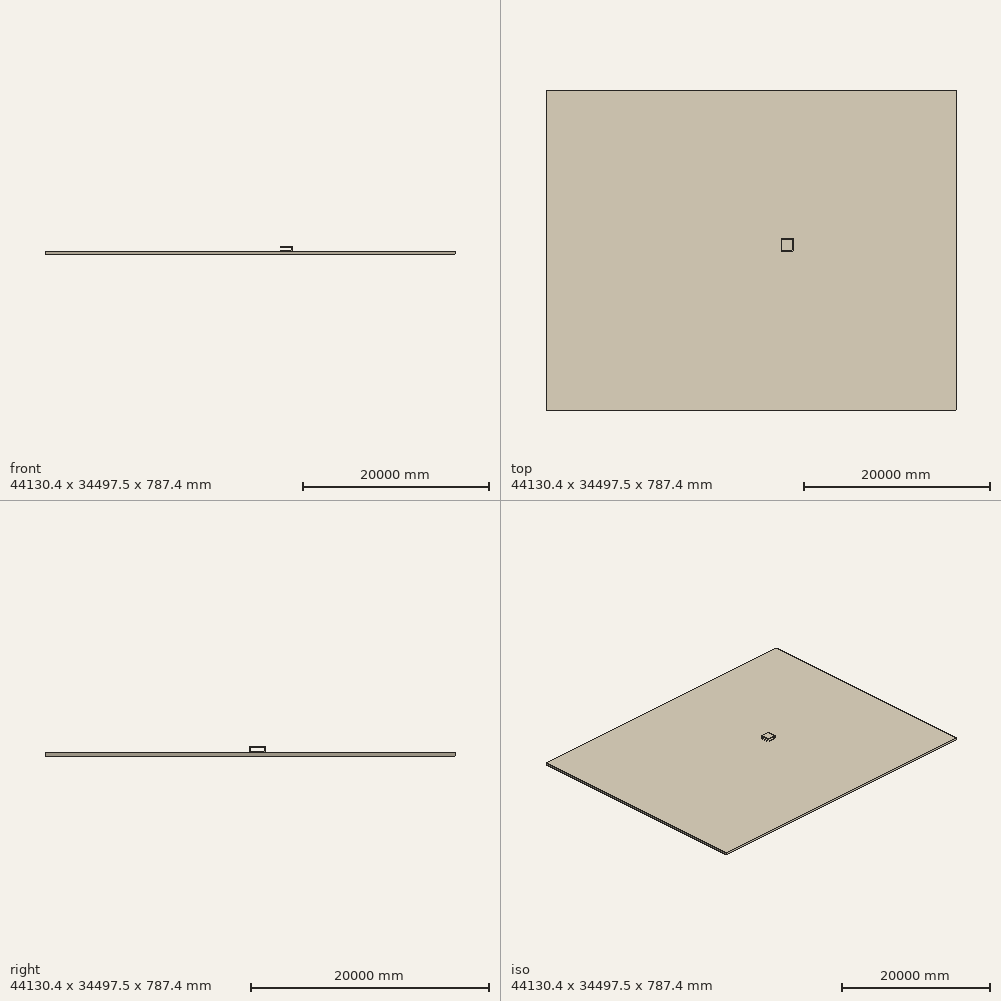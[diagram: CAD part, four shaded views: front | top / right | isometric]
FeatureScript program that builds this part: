
annotation { "Feature Type Name" : "Feature", "Feature Type Description" : "" }
export const myFeature = defineFeature(function(context is Context, id is Id, definition is map)
    precondition{}
    {
        {
            var Q0;
            Q0=qCreatedBy(makeId("Top.planeOp"),FACE);
            var sketch = newSketch(context, id + "F0", { "sketchPlane" : qUnion([Q0])});
            skLineSegment(sketch, "E0", {"start": v(0, 0) * mm, "end": v(0, 1320.8) * mm});
            skLineSegment(sketch, "E1", {"start": v(0, 0) * mm, "end": v(1301.47, 0) * mm});
            skLineSegment(sketch, "E2", {"start": v(0, 1320.8) * mm, "end": v(1301.47, 1320.8) * mm});
            skLineSegment(sketch, "E3", {"start": v(1301.47, 1320.8) * mm, "end": v(1301.47, 0) * mm});
            skLineSegment(sketch, "E4", {"start": v(50.8, 50.8) * mm, "end": v(1250.67, 50.8) * mm});
            skLineSegment(sketch, "E5", {"start": v(1250.67, 50.8) * mm, "end": v(1250.67, 1270) * mm});
            skLineSegment(sketch, "E6", {"start": v(1250.67, 1270) * mm, "end": v(50.8, 1270) * mm});
            skLineSegment(sketch, "E7", {"start": v(50.8, 1270) * mm, "end": v(50.8, 50.8) * mm});
            skLineSegment(sketch, "E8", {"start": v(387.94, 1270) * mm, "end": v(387.94, 1320.8) * mm, "construction": true});
            skLineSegment(sketch, "E9", {"start": v(1250.67, 761.64) * mm, "end": v(1301.47, 761.64) * mm, "construction": true});
            skLineSegment(sketch, "E10", {"start": v(50.8, 721.4) * mm, "end": v(0, 721.4) * mm, "construction": true});
            skLineSegment(sketch, "E11", {"start": v(704.11, 50.8) * mm, "end": v(704.11, 0) * mm, "construction": true});
            skSolve(sketch);
        }
        {
            var Q0;
            Q0=makeQuery(id+"F0.imprint","IMPRINT",FACE,{"disambiguationData":[TD([[makeQuery(id+"F0.imprint","IMPRINT",EDGE,{"derivedFrom":sQuery(id+"F0.wireOp",EDGE,"E0")}),-1.0]])]});
            extrude(context, id + "F1", {"entities" : qUnion([Q0]), "depth" : 50.8 * mm});
        }
        {
            var Q0;
            Q0=makeQuery(id+"F1.opExtrude","CAP_FACE",FACE,{"disambiguationData":[OSD([sQuery(id+"F0.wireOp",EDGE,"E0"),sQuery(id+"F0.wireOp",EDGE,"E1"),sQuery(id+"F0.wireOp",EDGE,"E2"),sQuery(id+"F0.wireOp",EDGE,"E3"),sQuery(id+"F0.wireOp",EDGE,"E4"),sQuery(id+"F0.wireOp",EDGE,"E5"),sQuery(id+"F0.wireOp",EDGE,"E6"),sQuery(id+"F0.wireOp",EDGE,"E7")])],"isStart":false});
            var sketch = newSketch(context, id + "F2", { "sketchPlane" : qUnion([Q0])});
            skLineSegment(sketch, "E12", {"start": v(1250.67, 50.8) * mm, "end": v(1250.67, 0) * mm});
            skLineSegment(sketch, "E13", {"start": v(1301.47, 0) * mm, "end": v(1250.67, 0) * mm});
            skLineSegment(sketch, "E14", {"start": v(1250.67, 50.8) * mm, "end": v(1301.47, 50.8) * mm});
            skLineSegment(sketch, "E15", {"start": v(1301.47, 0) * mm, "end": v(1301.47, 50.8) * mm});
            skLineSegment(sketch, "E16", {"start": v(1250.67, 1270) * mm, "end": v(1301.47, 1270) * mm});
            skLineSegment(sketch, "E17", {"start": v(1301.47, 1320.8) * mm, "end": v(1301.47, 1270) * mm});
            skLineSegment(sketch, "E18", {"start": v(1301.47, 1320.8) * mm, "end": v(1250.67, 1320.8) * mm});
            skLineSegment(sketch, "E19", {"start": v(1250.67, 1270) * mm, "end": v(1250.67, 1320.8) * mm});
            skLineSegment(sketch, "E20", {"start": v(0, 1320.8) * mm, "end": v(50.8, 1320.8) * mm});
            skLineSegment(sketch, "E21", {"start": v(50.8, 1270) * mm, "end": v(50.8, 1320.8) * mm});
            skLineSegment(sketch, "E22", {"start": v(50.8, 1270) * mm, "end": v(0, 1270) * mm});
            skLineSegment(sketch, "E23", {"start": v(0, 1320.8) * mm, "end": v(0, 1270) * mm});
            skLineSegment(sketch, "E24", {"start": v(50.8, 50.8) * mm, "end": v(0, 50.8) * mm});
            skLineSegment(sketch, "E25", {"start": v(0, 50.8) * mm, "end": v(0, 0) * mm});
            skLineSegment(sketch, "E26", {"start": v(0, 0) * mm, "end": v(50.8, 0) * mm});
            skLineSegment(sketch, "E27", {"start": v(50.8, 0) * mm, "end": v(50.8, 50.8) * mm});
            skSolve(sketch);
        }
        {
            var Q0;
            Q0=makeQuery(id+"F2.imprint","IMPRINT",FACE,{"disambiguationData":[TD([[makeQuery(id+"F2.imprint","IMPRINT",EDGE,{"derivedFrom":sQuery(id+"F2.wireOp",EDGE,"E24")}),1.0]])]});
            var Q1;
            Q1=makeQuery(id+"F2.imprint","IMPRINT",FACE,{"disambiguationData":[TD([[makeQuery(id+"F2.imprint","IMPRINT",EDGE,{"derivedFrom":sQuery(id+"F2.wireOp",EDGE,"E20")}),-1.0]])]});
            var Q2;
            Q2=makeQuery(id+"F2.imprint","IMPRINT",FACE,{"disambiguationData":[TD([[makeQuery(id+"F2.imprint","IMPRINT",EDGE,{"derivedFrom":sQuery(id+"F2.wireOp",EDGE,"E16")}),1.0]])]});
            var Q3;
            Q3=makeQuery(id+"F2.imprint","IMPRINT",FACE,{"disambiguationData":[TD([[makeQuery(id+"F2.imprint","IMPRINT",EDGE,{"derivedFrom":sQuery(id+"F2.wireOp",EDGE,"E12")}),1.0]])]});
            extrude(context, id + "F3", {"entities" : qUnion([Q0, Q1, Q2, Q3]), "operationType" : NewBodyOperationType.ADD, "depth" : 355.6 * mm});
        }
        {
            var Q0;
            Q0=makeQuery(id+"F3.opExtrude","CAP_FACE",FACE,{"disambiguationData":[OSD([sQuery(id+"F2.wireOp",EDGE,"E24"),sQuery(id+"F2.wireOp",EDGE,"E25"),sQuery(id+"F2.wireOp",EDGE,"E26"),sQuery(id+"F2.wireOp",EDGE,"E27")])],"isStart":false});
            var sketch = newSketch(context, id + "F4", { "sketchPlane" : qUnion([Q0])});
            skSolve(sketch);
        }
        {
            var Q0;
            Q0=makeQuery(id+"F4.imprint","IMPRINT",FACE,{"disambiguationData":[TD([[makeQuery(id+"F4.imprint","IMPRINT",EDGE,{"derivedFrom":makeQuery(id+"F3.opExtrude","CAP_EDGE",EDGE,{"disambiguationData":[OSD([sQuery(id+"F2.wireOp",EDGE,"E24")])],"isStart":false})}),1.0]])]});
            var sketch = newSketch(context, id + "F5", { "sketchPlane" : qUnion([Q0])});
            skLineSegment(sketch, "E28.bottom", {"start": v(0, 0) * mm, "end": v(1301.47, 0) * mm});
            skLineSegment(sketch, "E28.top", {"start": v(0, 1320.8) * mm, "end": v(1301.47, 1320.8) * mm});
            skLineSegment(sketch, "E28.left", {"start": v(0, 0) * mm, "end": v(0, 1320.8) * mm});
            skLineSegment(sketch, "E28.right", {"start": v(1301.47, 0) * mm, "end": v(1301.47, 1320.8) * mm});
            skLineSegment(sketch, "E29", {"start": v(0, 0) * mm, "end": v(50.8, 50.8) * mm, "construction": true});
            skLineSegment(sketch, "E30.bottom", {"start": v(50.8, 50.8) * mm, "end": v(1250.67, 50.8) * mm});
            skLineSegment(sketch, "E30.top", {"start": v(50.8, 1270) * mm, "end": v(1250.67, 1270) * mm});
            skLineSegment(sketch, "E30.left", {"start": v(50.8, 50.8) * mm, "end": v(50.8, 1270) * mm});
            skLineSegment(sketch, "E30.right", {"start": v(1250.67, 50.8) * mm, "end": v(1250.67, 1270) * mm});
            skSolve(sketch);
        }
        {
            var Q0;
            Q0 = qSketchRegion(id + "F5", true);
            extrude(context, id + "F6", {"entities" : qUnion([Q0]), "operationType" : NewBodyOperationType.ADD, "depth" : 50.8 * mm});
        }
        {
            var Q0;
            Q0=makeQuery(id+"F6.opExtrude","CAP_FACE",FACE,{"disambiguationData":[OSD([sQuery(id+"F5.wireOp",EDGE,"E28.bottom"),sQuery(id+"F5.wireOp",EDGE,"E28.top"),sQuery(id+"F5.wireOp",EDGE,"E28.left"),sQuery(id+"F5.wireOp",EDGE,"E28.right"),sQuery(id+"F5.wireOp",EDGE,"E30.bottom"),sQuery(id+"F5.wireOp",EDGE,"E30.top"),sQuery(id+"F5.wireOp",EDGE,"E30.left"),sQuery(id+"F5.wireOp",EDGE,"E30.right")])],"isStart":false});
            var sketch = newSketch(context, id + "F7", { "sketchPlane" : qUnion([Q0])});
            skLineSegment(sketch, "E31.bottom", {"start": v(50.8, 50.8) * mm, "end": v(1250.67, 50.8) * mm});
            skLineSegment(sketch, "E31.top", {"start": v(50.8, 1270) * mm, "end": v(1250.67, 1270) * mm});
            skLineSegment(sketch, "E31.left", {"start": v(50.8, 50.8) * mm, "end": v(50.8, 1270) * mm});
            skLineSegment(sketch, "E31.right", {"start": v(1250.67, 50.8) * mm, "end": v(1250.67, 1270) * mm});
            skSolve(sketch);
        }
        {
            var Q0;
            Q0 = qSketchRegion(id + "F7", true);
            extrude(context, id + "F8", {"entities" : qUnion([Q0]), "oppositeDirection" : true, "depth" : 12.7 * mm});
        }
        {
            var Q0;
            Q0=makeQuery(id+"F1.opExtrude","CAP_FACE",FACE,{"disambiguationData":[OSD([sQuery(id+"F0.wireOp",EDGE,"E0"),sQuery(id+"F0.wireOp",EDGE,"E1"),sQuery(id+"F0.wireOp",EDGE,"E2"),sQuery(id+"F0.wireOp",EDGE,"E3"),sQuery(id+"F0.wireOp",EDGE,"E4"),sQuery(id+"F0.wireOp",EDGE,"E5"),sQuery(id+"F0.wireOp",EDGE,"E6"),sQuery(id+"F0.wireOp",EDGE,"E7")])],"isStart":true});
            cPlane(context, id + "F9", {"entities" : qUnion([Q0]), "cplaneType" : CPlaneType.OFFSET, "offset" : 25.4 * mm, "width" : 152.4 * mm, "height" : 152.4 * mm});
        }
        {
            var Q0;
            Q0=qCreatedBy(id+"F9.planeOp",FACE);
            var sketch = newSketch(context, id + "F10", { "sketchPlane" : qUnion([Q0])});
            skLineSegment(sketch, "E32", {"start": v(0, 0) * mm, "end": v(0, 17176.6) * mm, "construction": true});
            skLineSegment(sketch, "E33", {"start": v(0, 17176.6) * mm, "end": v(-25275.7, 17176.6) * mm, "construction": true});
            skLineSegment(sketch, "E34.bottom", {"start": v(-25275.7, 17176.6) * mm, "end": v(18854.66, 17176.6) * mm});
            skLineSegment(sketch, "E34.top", {"start": v(-25275.7, -17320.86) * mm, "end": v(18854.66, -17320.86) * mm});
            skLineSegment(sketch, "E34.left", {"start": v(-25275.7, 17176.6) * mm, "end": v(-25275.7, -17320.86) * mm});
            skLineSegment(sketch, "E34.right", {"start": v(18854.66, 17176.6) * mm, "end": v(18854.66, -17320.86) * mm});
            skSolve(sketch);
        }
        {
            var Q0;
            Q0=makeQuery(id+"F10.imprint","IMPRINT",FACE,{"disambiguationData":[TD([[makeQuery(id+"F10.imprint","IMPRINT",EDGE,{"derivedFrom":sQuery(id+"F10.wireOp",EDGE,"E34.bottom")}),-1.0]])]});
            var Q1;
            Q1 = qSketchRegion(id + "F10", true);
            extrude(context, id + "F11", {"entities" : qUnion([Q0, Q1]), "depth" : 304.8 * mm});
        }
    });
